FCSTD DOCUMENT  (FreeCAD 0.20R26155 (Git))
Label: SNESconnector
License: All rights reserved
LicenseURL: http://en.wikipedia.org/wiki/All_rights_reserved
objects: Sketcher::SketchObject×2, PartDesign::Body×1
note: 3 computed .brp shape members not serialized (recipe doc carries the construction recipe); baked Part::Feature solids carry a one-line shape summary decoded from their .brp

FEATURE [Sketcher::SketchObject] Sketch
  FullyConstrained = true
  MapMode = 5
  Support = -> [XY_Plane]
  sketch-geometry (4):
    g0: LineSegment StartX=-68.25 StartY=4.5 StartZ=0 EndX=68.25 EndY=4.5 EndZ=0
    g1: LineSegment StartX=68.25 StartY=4.5 StartZ=0 EndX=68.25 EndY=-4.5 EndZ=0
    g2: LineSegment StartX=68.25 StartY=-4.5 StartZ=0 EndX=-68.25 EndY=-4.5 EndZ=0
    g3: LineSegment StartX=-68.25 StartY=-4.5 StartZ=0 EndX=-68.25 EndY=4.5 EndZ=0
  constraints (10):
    c: Coincident(g0,g1)
    c: Coincident(g1,g2)
    c: Coincident(g2,g3)
    c: Coincident(g3,g0)
    c: Horizontal(g2)
    c: Vertical(g1)
    c: Symmetric(g0,g0,g-2)
    c: Symmetric(g2,g0,g-1)
    c: DistanceY(g3,g3) = 9
    c: DistanceX(g0,g0) = 136.5
FEATURE [Sketcher::SketchObject] Sketch001
  ExternalGeometry = -> [Sketch]
  FullyConstrained = false
  MapMode = 5
  Support = -> [XY_Plane]
  sketch-geometry (3):
    g0: LineSegment StartX=-70.5154 StartY=2.18923 StartZ=0 EndX=71.1383 EndY=2.18923 EndZ=0
    g1: LineSegment StartX=-70.4695 StartY=-2.81077 StartZ=0 EndX=71.291 EndY=-2.81077 EndZ=0
    g2: LineSegment StartX=-48.0019 StartY=2.18923 StartZ=0 EndX=-48.0019 EndY=-2.81077 EndZ=0
  constraints (6):
    c: Horizontal(g0)
    c: Horizontal(g1)
    c: DistanceY(g1,g0) = 5
    c: PointOnObject(g2,g0)
    c: PointOnObject(g2,g1)
    c: Vertical(g2)
FEATURE [PartDesign::Body] Body
  Group = -> [Sketch,Sketch001]
  Origin = -> Origin
